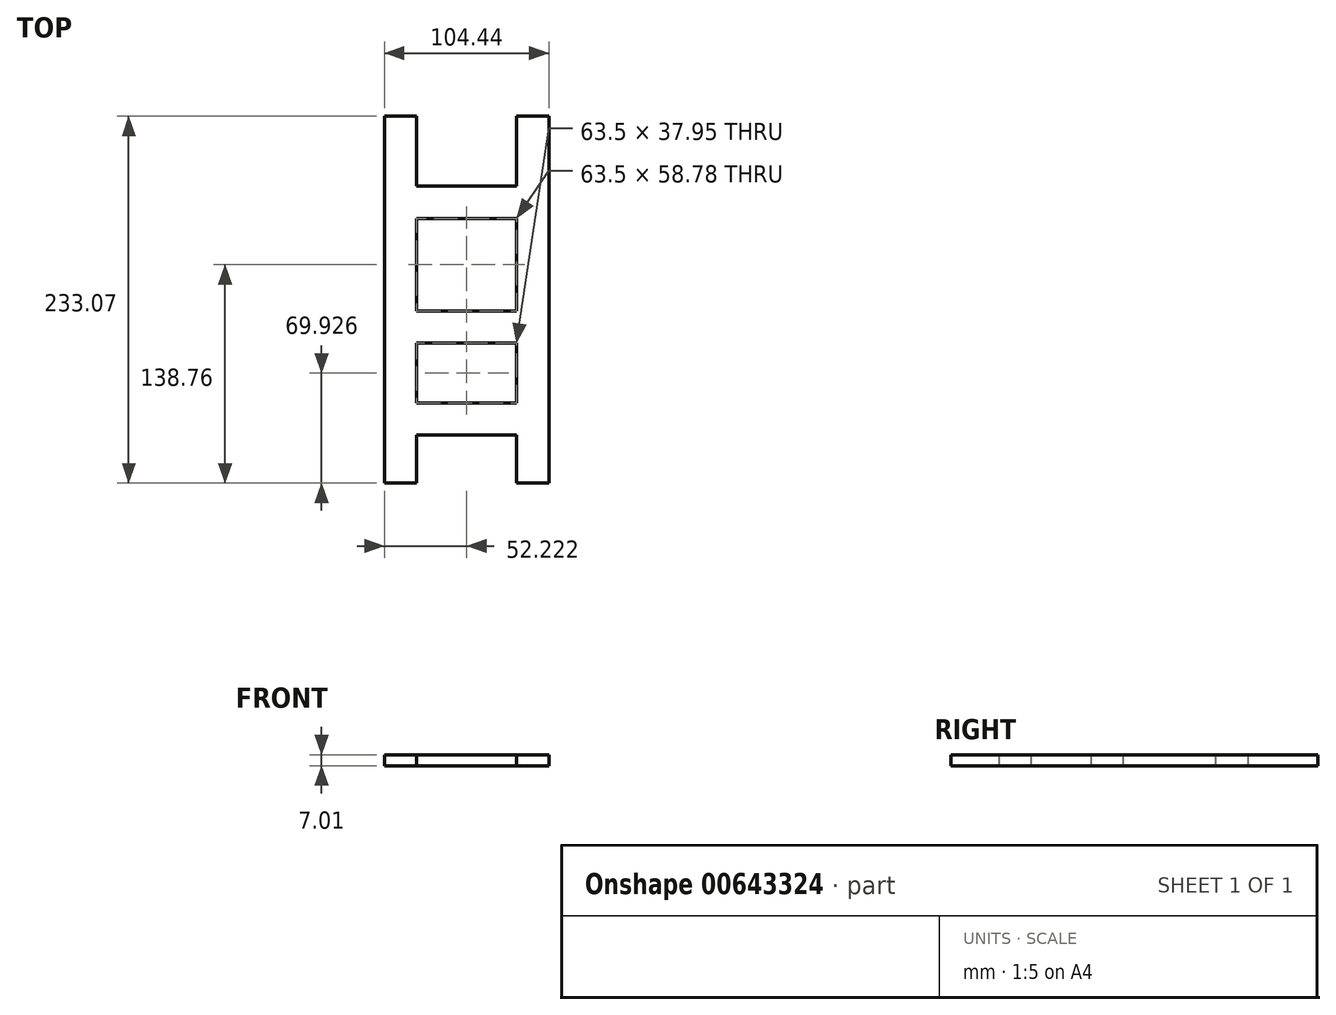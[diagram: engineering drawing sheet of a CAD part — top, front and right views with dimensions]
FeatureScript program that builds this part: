
annotation { "Feature Type Name" : "Feature", "Feature Type Description" : "" }
export const myFeature = defineFeature(function(context is Context, id is Id, definition is map)
    precondition{}
    {
        {
            var Q0;
            Q0=qCreatedBy(makeId("Top.planeOp"),FACE);
            var sketch = newSketch(context, id + "F0", { "sketchPlane" : qUnion([Q0])});
            skLineSegment(sketch, "E0.bottom", {"start": v(-76.94, 123.52) * mm, "end": v(-56.47, 123.52) * mm});
            skLineSegment(sketch, "E0.top", {"start": v(-76.94, -109.55) * mm, "end": v(-56.47, -109.55) * mm});
            skLineSegment(sketch, "E0.left", {"start": v(-76.94, 123.52) * mm, "end": v(-76.94, -109.55) * mm});
            skLineSegment(sketch, "E0.right", {"start": v(-56.47, 123.52) * mm, "end": v(-56.47, -109.55) * mm});
            skLineSegment(sketch, "E1.bottom", {"start": v(-56.47, 79.07) * mm, "end": v(-24.72, 79.07) * mm});
            skLineSegment(sketch, "E1.top", {"start": v(-56.47, 58.6) * mm, "end": v(-24.72, 58.6) * mm});
            skLineSegment(sketch, "E1.left", {"start": v(-56.47, 79.07) * mm, "end": v(-56.47, 58.6) * mm});
            skLineSegment(sketch, "E1.right", {"start": v(-24.72, 79.07) * mm, "end": v(-24.72, 58.6) * mm});
            skLineSegment(sketch, "E2", {"start": v(-76.94, 0) * mm, "end": v(-56.47, 0) * mm, "construction": true});
            skLineSegment(sketch, "E3.MirrorCS", {"start": v(-56.47, -58.6) * mm, "end": v(-24.72, -58.6) * mm});
            skLineSegment(sketch, "E4.MirrorCS", {"start": v(-56.47, -79.07) * mm, "end": v(-24.72, -79.07) * mm});
            skLineSegment(sketch, "E5.MirrorCS", {"start": v(-24.72, -79.07) * mm, "end": v(-24.72, -58.6) * mm});
            skLineSegment(sketch, "E6.MirrorCS", {"start": v(27.5, 123.52) * mm, "end": v(27.5, -109.55) * mm});
            skLineSegment(sketch, "E7.MirrorCS", {"start": v(27.5, 123.52) * mm, "end": v(7.03, 123.52) * mm});
            skLineSegment(sketch, "E8.MirrorCS", {"start": v(7.03, 123.52) * mm, "end": v(7.03, -109.55) * mm});
            skLineSegment(sketch, "E9.MirrorCS", {"start": v(7.03, 79.07) * mm, "end": v(7.03, 58.6) * mm});
            skLineSegment(sketch, "E10.MirrorCS", {"start": v(7.03, 79.07) * mm, "end": v(-24.72, 79.07) * mm});
            skLineSegment(sketch, "E11.MirrorCS", {"start": v(7.03, 58.6) * mm, "end": v(-24.72, 58.6) * mm});
            skLineSegment(sketch, "E12.MirrorCS", {"start": v(7.03, -58.6) * mm, "end": v(-24.72, -58.6) * mm});
            skLineSegment(sketch, "E13.MirrorCS", {"start": v(7.03, -79.07) * mm, "end": v(-24.72, -79.07) * mm});
            skLineSegment(sketch, "E14.MirrorCS", {"start": v(27.5, -109.55) * mm, "end": v(7.03, -109.55) * mm});
            skLineSegment(sketch, "E15.bottom", {"start": v(-56.47, -0.18) * mm, "end": v(7.03, -0.18) * mm});
            skLineSegment(sketch, "E15.top", {"start": v(-56.47, -20.65) * mm, "end": v(7.03, -20.65) * mm});
            skLineSegment(sketch, "E15.left", {"start": v(-56.47, -0.18) * mm, "end": v(-56.47, -20.65) * mm});
            skLineSegment(sketch, "E15.right", {"start": v(7.03, -0.18) * mm, "end": v(7.03, -20.65) * mm});
            skSolve(sketch);
        }
        {
            var Q0;
            {var subQ1=sQuery(id+"F0.wireOp",EDGE,"E0.bottom");Q0=makeQuery(id+"F0.imprint","IMPRINT",FACE,{"disambiguationData":[TD([[makeQuery(id+"F0.imprint","IMPRINT",EDGE,{"derivedFrom":subQ1}),-1.0]])]});}
            var Q1;
            Q1=makeQuery(id+"F0.imprint","IMPRINT",FACE,{"disambiguationData":[TD([[makeQuery(id+"F0.imprint","IMPRINT",EDGE,{"derivedFrom":sQuery(id+"F0.wireOp",EDGE,"E1.bottom")}),-1.0]])]});
            var Q2;
            Q2=makeQuery(id+"F0.imprint","IMPRINT",FACE,{"disambiguationData":[TD([[makeQuery(id+"F0.imprint","IMPRINT",EDGE,{"derivedFrom":sQuery(id+"F0.wireOp",EDGE,"E1.right")}),1.0]])]});
            var Q3;
            Q3=makeQuery(id+"F0.imprint","IMPRINT",FACE,{"disambiguationData":[TD([[makeQuery(id+"F0.imprint","IMPRINT",EDGE,{"derivedFrom":sQuery(id+"F0.wireOp",EDGE,"E6.MirrorCS")}),-1.0]])]});
            var Q4;
            Q4=makeQuery(id+"F0.imprint","IMPRINT",FACE,{"disambiguationData":[TD([[makeQuery(id+"F0.imprint","IMPRINT",EDGE,{"derivedFrom":sQuery(id+"F0.wireOp",EDGE,"E15.bottom")}),-1.0]])]});
            var Q5;
            {var subQ0=sQuery(id+"F0.wireOp",EDGE,"E3.MirrorCS");Q5=makeQuery(id+"F0.imprint","IMPRINT",FACE,{"disambiguationData":[TD([[makeQuery(id+"F0.imprint","IMPRINT",EDGE,{"derivedFrom":subQ0}),-1.0]])]});}
            var Q6;
            Q6=makeQuery(id+"F0.imprint","IMPRINT",FACE,{"disambiguationData":[TD([[makeQuery(id+"F0.imprint","IMPRINT",EDGE,{"derivedFrom":sQuery(id+"F0.wireOp",EDGE,"E5.MirrorCS")}),-1.0]])]});
            extrude(context, id + "F1", {"entities" : qUnion([Q0, Q1, Q2, Q3, Q4, Q5, Q6]), "depth" : 7 * mm, "offsetDistance" : 25.4 * mm});
        }
    });
